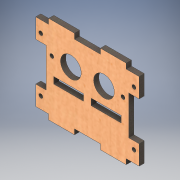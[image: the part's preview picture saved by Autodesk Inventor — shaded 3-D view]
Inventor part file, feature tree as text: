
AUTODESK INVENTOR PART (.ipt)
format: ipt  version: 2019 (Build 230136000, 136)  size: 210,944 bytes
history: native  units: mm
features: sketch x5, hole x3, extrude x2, other x1
ambient origin geometry x8: Origin, YZ Plane, XZ Plane, XY Plane, X Axis, Y Axis, Z Axis, Center Point
bodies: Body1 (feature_tree)
feature tree (11):
  other  "Твердое тело1"
  extrude  "Выдавливание1"  Depth=4.0mm
  hole  "Отверстие1"  [1 undecoded]
  hole  "Отверстие2"  [1 undecoded]
  hole  "Отверстие3"  [1 undecoded]
  extrude  "Выдавливание2"  Depth=15.0mm
  sketch  "Эскиз1"
  sketch  "Эскиз2"
  sketch  "Эскиз3"
  sketch  "Эскиз4"
  sketch  "Эскиз5"
note: 3 required parameter values undecoded (feature->parameter linkage not recoverable at this tier; creation-order binding heuristic only, values carry confidence <= 0.55)
